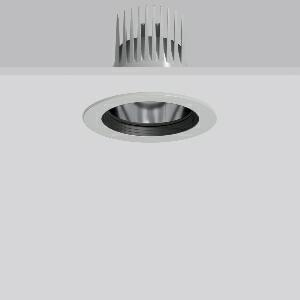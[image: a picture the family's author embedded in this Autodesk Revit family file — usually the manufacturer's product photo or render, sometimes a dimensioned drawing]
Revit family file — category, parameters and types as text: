
# Revit family: heledon_maxi_e_901765_004_530f
name_source: partatom
category: Lighting Fixtures
units: mm (PartAtom-declared; Revit-internal decimal feet)

## family parameters
Cut with Voids When Loaded = No
Host = Face
Light Source = No
Part Type = Normal
Room Calculation Point = No
Round Connector Dimension = Use Diameter
Shared = No

## types (1)
- HELEDON maxi E (1 x LED Modul 930, 4350 lm, 3000)
    Apparent Load = 35 VA
    Approval mark = CE
    CIE Flux Codes = 100 100 100 100 100
    Color Rendering = 90
    Color Temperature = 3000
    Default Elevation = 1800 mm
    Description = Series: HELEDON maxi
Round recessed downlight. Housing: die-cast aluminium, powder-coated. Black plastic ring and recessed LED to prevent glare from the side. Optical assembly with reflector made of MIRO-Silver with 98% total light reflection for outstanding efficiency - can be changed without tools. Best colour rendering index Ra>90. Suitable for Recessed ceiling mounting. Installation without tools thanks to spring fastening system. Including separate LED converter with connecting cable 600 mm.High quality converter without flickering and stroboscopic effect. Through-wiring box (5 pole) available as accessory. The following accessories can be mounted without use of tools: interchangeable lenses, decorative glasses, honeycomb louvre, clear and frosted diffusers, white interchangeable plastic ring. 
Colour: silver
Diameter: 162 mm
Height: 3 mm
Cut-out diameter: 152 mm
Recess height: 200 mm
Luminaire: recess height: 135 mm
Lamp: LED
Socket: without socket
Colour temperature: 3000K
Colour rendering index (CRI): 92
System power: 35 W
Rated luminous flux: 4350 lm
Luminous efficiency: 124 lm/W
Control gear: Regulated power supply
Protection class: II
Type of protection: IP 20
    Height = 0 mm  [stored 0 ft]
    Lamp = 1 x LED Modul 930
    Lamp Light Flux = 4350 lm
    Lamp count = 1
    Length = 162 mm
    Lifetime = 50000 h
    Luminous efficacy = 124 lm/W
    Manufacturer = RZB
    ModVariant = No
    Model = 901765.004
    Mounting Place = Ceiling
    Mounting Type = Recessed
    Number of Poles = 1
    OnlyDefault = Yes
    Power Factor = 1
    Product Name = HELEDON maxi E
    Product group = Recessed downlights
    ProductGroupID = 402
    Protection Class = Protection class II
    Protection Degree = IP 20
    RLX_Detail_Level = 1
    RLX_Emergency_Light_Flux = 0 lm
    RLX_Emergency_Type = 0
    RLX_Emergency_Type_DB = No
    RlxData = <blob elided: 118685 chars, md5=c31cfd71>
    Socket = socket
    Standby Power = 0 W
    System Light Flux = 4350 lm
    System Power = 35 W
    Type Comments = Product without accessories
    Type Image = 901662.004.jpg
    URL = http://relux.com
    VarID = ---
    Voltage = 230 V
    Voltage Range = 220-240 V
    Weight = 0.00 kg
    Width = 0 mm  [stored 0 ft]

note: [stored X ft] marks values corroborated as IEEE doubles in the binary element streams (Revit-internal decimal feet)

## geometry (parser evidence)
native form markers: Blend x4, Sweep x11
no freeform markers — native parametric forms only
